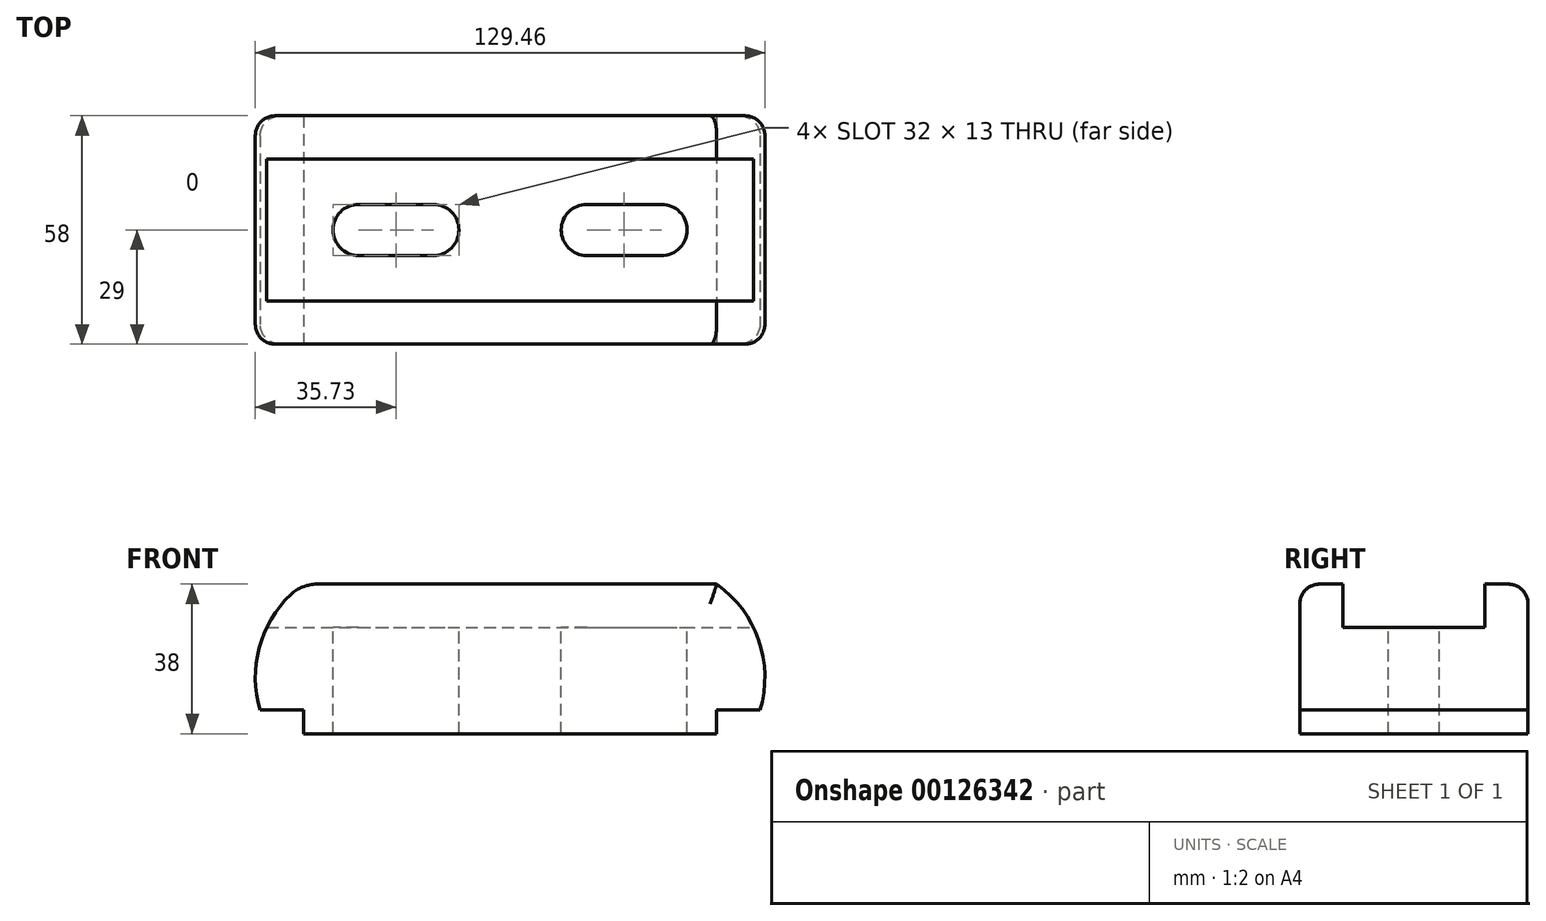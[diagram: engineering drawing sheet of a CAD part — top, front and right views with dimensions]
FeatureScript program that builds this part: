
annotation { "Feature Type Name" : "Feature", "Feature Type Description" : "" }
export const myFeature = defineFeature(function(context is Context, id is Id, definition is map)
    precondition{}
    {
        {
            var Q0;
            Q0=qCreatedBy(makeId("Front.planeOp"),FACE);
            var sketch = newSketch(context, id + "F0", { "sketchPlane" : qUnion([Q0])});
            skLineSegment(sketch, "E0", {"start": v(0, 0) * mm, "end": v(105, 0) * mm});
            skLineSegment(sketch, "E1", {"start": v(0, 0) * mm, "end": v(0, 6) * mm});
            skLineSegment(sketch, "E2", {"start": v(105, 0) * mm, "end": v(105, 6) * mm});
            skLineSegment(sketch, "E3", {"start": v(0, 6) * mm, "end": v(-11, 6) * mm});
            skLineSegment(sketch, "E4", {"start": v(105, 6) * mm, "end": v(116, 6) * mm});
            skArc(sketch, "E5", {"start": v(-3.18, 35.39) * mm, "mid": v(-11.25, 21.8) * mm, "end": v(-11, 6) * mm});
            skArc(sketch, "E6", {"start": v(116, 6) * mm, "mid": v(115.65, 23.77) * mm, "end": v(105, 38) * mm});
            skLineSegment(sketch, "E7", {"start": v(3.37, 38) * mm, "end": v(105, 38) * mm});
            skPoint(sketch, "E8.visualSharp", {"position": v(0, 38) * mm});
            skArc(sketch, "E8.filletArc", {"start": v(3.37, 38) * mm, "mid": v(-0.15, 37.32) * mm, "end": v(-3.18, 35.39) * mm});
            skSolve(sketch);
        }
        {
            var Q0;
            Q0=makeQuery(id+"F0.imprint","IMPRINT",FACE,{"disambiguationData":[TD([[makeQuery(id+"F0.imprint","IMPRINT",EDGE,{"derivedFrom":sQuery(id+"F0.wireOp",EDGE,"E0")}),1.0]])]});
            extrude(context, id + "F1", {"entities" : qUnion([Q0]), "oppositeDirection" : true, "depth" : 58 * mm});
        }
        {
            var Q0;
            Q0=makeQuery(id+"F1.opExtrude","SWEPT_FACE",FACE,{"disambiguationData":[OSD([sQuery(id+"F0.wireOp",EDGE,"E7")])]});
            var sketch = newSketch(context, id + "F2", { "sketchPlane" : qUnion([Q0])});
            skLineSegment(sketch, "E9", {"start": v(-14.75, 47) * mm, "end": v(105, 47) * mm});
            skLineSegment(sketch, "E10", {"start": v(105, 11) * mm, "end": v(-14.75, 11) * mm});
            skLineSegment(sketch, "E11", {"start": v(-14.75, 11) * mm, "end": v(-14.75, 47) * mm});
            skLineSegment(sketch, "E12", {"start": v(105, 47) * mm, "end": v(126.72, 47) * mm});
            skLineSegment(sketch, "E13", {"start": v(126.72, 47) * mm, "end": v(126.72, 11) * mm});
            skLineSegment(sketch, "E14", {"start": v(126.72, 11) * mm, "end": v(105, 11) * mm});
            skSolve(sketch);
        }
        {
            var Q0;
            {var subQ0=sQuery(id+"F2.wireOp",EDGE,"JVOvwiuQ-vAFm-lWZL-3nb3-qFpoUzjz7ExW");Q0=makeQuery(id+"F2.imprint","IMPRINT",FACE,{"disambiguationData":[TD([[makeQuery(id+"F2.imprint","IMPRINT",EDGE,{"derivedFrom":subQ0}),-1.0]])]});}
            var Q1;
            {var subQ0=sQuery(id+"F2.wireOp",EDGE,"E12");Q1=makeQuery(id+"F2.imprint","IMPRINT",FACE,{"disambiguationData":[TD([[makeQuery(id+"F2.imprint","IMPRINT",EDGE,{"derivedFrom":subQ0}),-1.0]])]});}
            var Q2;
            {var subQ0=sQuery(id+"F2.wireOp",EDGE,"E11");Q2=makeQuery(id+"F2.imprint","IMPRINT",FACE,{"disambiguationData":[TD([[makeQuery(id+"F2.imprint","IMPRINT",EDGE,{"derivedFrom":subQ0}),-1.0]])]});}
            var Q3;
            {var subQ0=sQuery(id+"F2.wireOp",EDGE,"E9");var subQ1=sQuery(id+"F0.wireOp",EDGE,"E7");var subQ4=makeQuery(id+"F1.opExtrude","SWEPT_EDGE",EDGE,{"disambiguationData":[OSD([subQ1,sQuery(id+"F0.wireOp",EDGE,"E8.filletArc")])]});var subQ5=makeQuery(id+"F2.imprint","INTERSECT",VERTEX,{"derivedFrom":[subQ4,subQ0]});Q3=makeQuery(id+"F2.imprint","IMPRINT",FACE,{"disambiguationData":[TD([[makeQuery(id+"F2.imprint","IMPRINT",EDGE,{"disambiguationData":[TD([[subQ5,-1.0]])],"derivedFrom":subQ0}),-1.0]])]});}
            extrude(context, id + "F3", {"entities" : qUnion([Q0, Q1, Q2, Q3]), "operationType" : NewBodyOperationType.REMOVE, "oppositeDirection" : true, "depth" : 11 * mm});
        }
        {
            var Q0;
            Q0=makeQuery(id+"F3.boolean.opBoolean","COPY",FACE,{"derivedFrom":makeQuery(id+"F3.opExtrude","CAP_FACE",FACE,{"disambiguationData":[OSD([sQuery(id+"F2.wireOp",EDGE,"E9"),sQuery(id+"F2.wireOp",EDGE,"E10"),sQuery(id+"F2.wireOp",EDGE,"E11"),sQuery(id+"F2.wireOp",EDGE,"E12"),sQuery(id+"F2.wireOp",EDGE,"E13"),sQuery(id+"F2.wireOp",EDGE,"E14")])],"isStart":false})});
            var sketch = newSketch(context, id + "F4", { "sketchPlane" : qUnion([Q0])});
            skLineSegment(sketch, "E15", {"start": v(-38.22, 29) * mm, "end": v(177.1, 29) * mm, "construction": true});
            skLineSegment(sketch, "E16", {"start": v(14, 35.5) * mm, "end": v(33, 35.5) * mm});
            skLineSegment(sketch, "E17", {"start": v(14, 22.5) * mm, "end": v(33, 22.5) * mm});
            skArc(sketch, "E18", {"start": v(14, 35.5) * mm, "mid": v(7.5, 29) * mm, "end": v(14, 22.5) * mm});
            skArc(sketch, "E19", {"start": v(33, 22.5) * mm, "mid": v(39.5, 29) * mm, "end": v(33, 35.5) * mm});
            skLineSegment(sketch, "E20", {"start": v(72, 35.5) * mm, "end": v(91, 35.5) * mm});
            skLineSegment(sketch, "E21", {"start": v(72, 22.5) * mm, "end": v(91, 22.5) * mm});
            skArc(sketch, "E22", {"start": v(72, 35.5) * mm, "mid": v(65.5, 29) * mm, "end": v(72, 22.5) * mm});
            skArc(sketch, "E23", {"start": v(91, 22.5) * mm, "mid": v(97.5, 29) * mm, "end": v(91, 35.5) * mm});
            skSolve(sketch);
        }
        {
            var Q0;
            Q0=makeQuery(id+"F4.imprint","IMPRINT",FACE,{"disambiguationData":[TD([[makeQuery(id+"F4.imprint","IMPRINT",EDGE,{"derivedFrom":sQuery(id+"F4.wireOp",EDGE,"E16")}),-1.0]])]});
            extrude(context, id + "F5", {"entities" : qUnion([Q0]), "operationType" : NewBodyOperationType.REMOVE, "oppositeDirection" : true, "depth" : 27 * mm});
        }
        {
            var Q0;
            Q0=makeQuery(id+"F4.imprint","IMPRINT",FACE,{"disambiguationData":[TD([[makeQuery(id+"F4.imprint","IMPRINT",EDGE,{"derivedFrom":sQuery(id+"F4.wireOp",EDGE,"E20")}),-1.0]])]});
            extrude(context, id + "F6", {"entities" : qUnion([Q0]), "operationType" : NewBodyOperationType.REMOVE, "oppositeDirection" : true, "depth" : 27 * mm});
        }
        {
            var Q0;
            Q0=makeQuery(id+"F1.opExtrude","CAP_EDGE",EDGE,{"disambiguationData":[OSD([sQuery(id+"F0.wireOp",EDGE,"E7")])],"isStart":true});
            var Q1;
            Q1=makeQuery(id+"F1.opExtrude","CAP_EDGE",EDGE,{"disambiguationData":[OSD([sQuery(id+"F0.wireOp",EDGE,"E6")])],"isStart":true});
            fillet(context, id + "F7", {"entities" : qUnion([Q0, Q1]), "radius" : 5 * mm, "tangentPropagation" : true, "allowEdgeOverflow" : false});
        }
        {
            var Q0;
            Q0=makeQuery(id+"F1.opExtrude","CAP_EDGE",EDGE,{"disambiguationData":[OSD([sQuery(id+"F0.wireOp",EDGE,"E6")])],"isStart":false});
            var Q1;
            Q1=makeQuery(id+"F1.opExtrude","CAP_EDGE",EDGE,{"disambiguationData":[OSD([sQuery(id+"F0.wireOp",EDGE,"E7")])],"isStart":false});
            fillet(context, id + "F8", {"entities" : qUnion([Q0, Q1]), "radius" : 5 * mm, "tangentPropagation" : true, "allowEdgeOverflow" : false});
        }
    });
